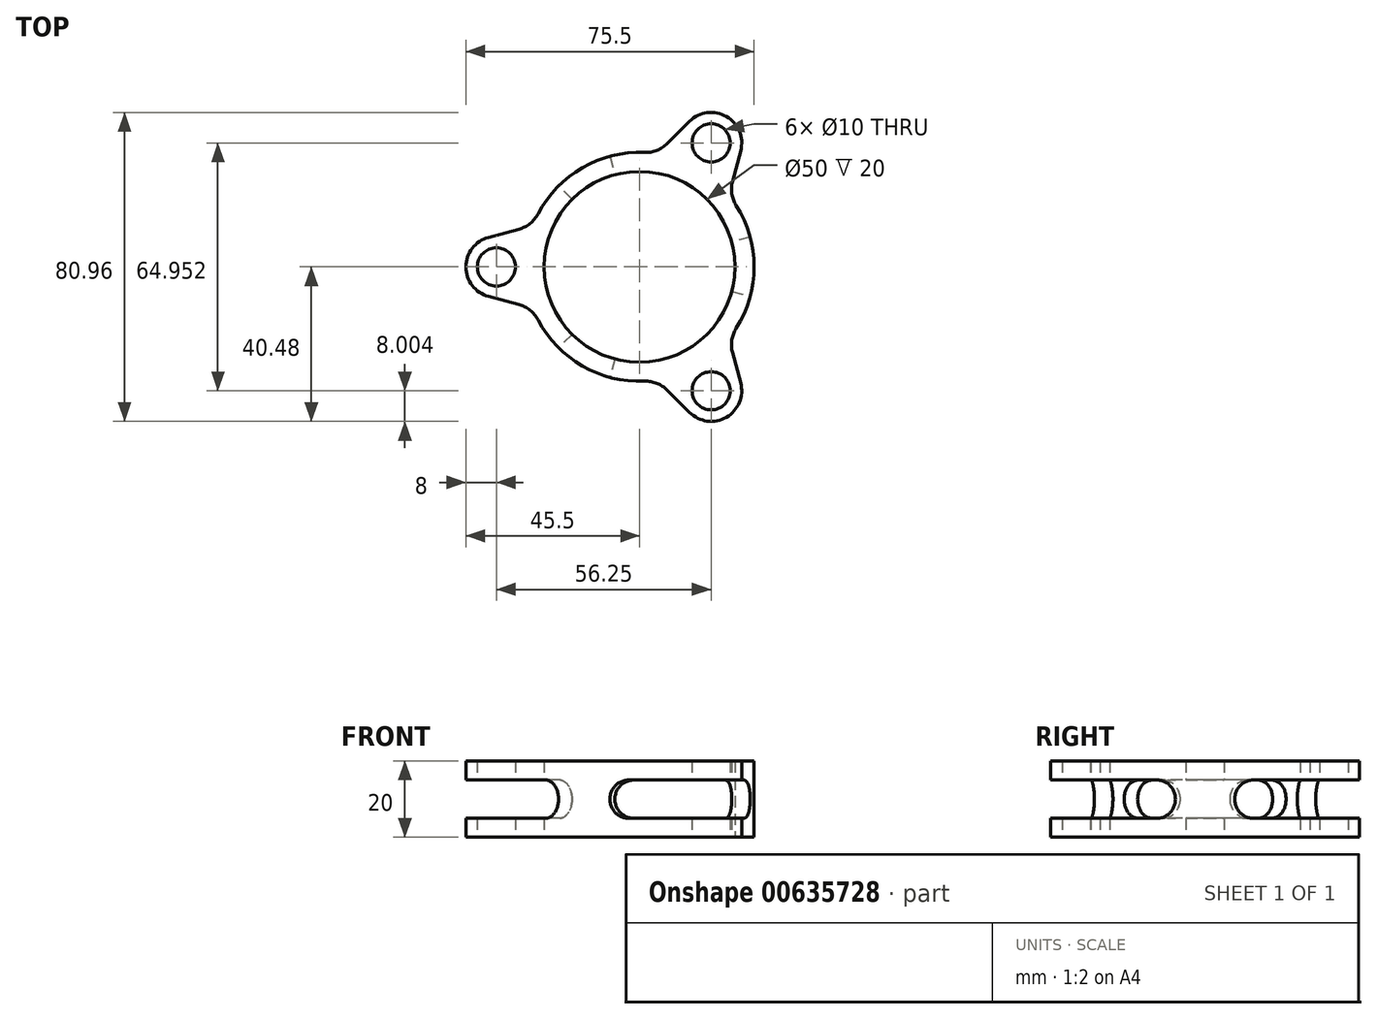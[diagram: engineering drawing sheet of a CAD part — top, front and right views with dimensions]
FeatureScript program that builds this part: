
annotation { "Feature Type Name" : "Feature", "Feature Type Description" : "" }
export const myFeature = defineFeature(function(context is Context, id is Id, definition is map)
    precondition{}
    {
        {
            assignVariable(context, id + "F0", {"name" : "CutoutThickness", "anyValue" : 10});
        }
        {
            assignVariable(context, id + "F1", {"name" : "CutoutFilletRadius", "anyValue" : getVariable(context, 'CutoutThickness') / 2});
        }
        {
            var Q0;
            Q0=qCreatedBy(makeId("Top.planeOp"),FACE);
            var sketch = newSketch(context, id + "F2", { "sketchPlane" : qUnion([Q0])});
            skCircle(sketch, "E0", {"center": v(0, 0) * mm, "radius": 25 * mm});
            skCircle(sketch, "E1", {"center": v(0, 0) * mm, "radius": 30 * mm});
            skLineSegment(sketch, "E2", {"start": v(-75, 0) * mm, "end": v(0, 0) * mm, "construction": true});
            skCircle(sketch, "E3", {"center": v(-37.5, 0) * mm, "radius": 5 * mm});
            skCircle(sketch, "E4", {"center": v(0, 0) * mm, "radius": 37.5 * mm, "construction": true});
            skLineSegment(sketch, "E5", {"start": v(-27.98, 10.83) * mm, "end": v(-39.57, 7.73) * mm});
            skLineSegment(sketch, "E6", {"start": v(-27.98, -10.83) * mm, "end": v(-39.57, -7.73) * mm});
            skArc(sketch, "E7", {"start": v(-39.57, 7.73) * mm, "mid": v(-45.5, 0) * mm, "end": v(-39.57, -7.73) * mm});
            skLineSegment(sketch, "E8.1.0", {"start": v(4.6, -29.64) * mm, "end": v(13.1, -38.13) * mm});
            skCircle(sketch, "E8.1.1", {"center": v(18.75, -32.48) * mm, "radius": 5 * mm});
            skLineSegment(sketch, "E8.1.2", {"start": v(23.37, -18.81) * mm, "end": v(26.48, -30.4) * mm});
            skArc(sketch, "E8.1.3", {"start": v(13.1, -38.13) * mm, "mid": v(22.75, -39.4) * mm, "end": v(26.48, -30.4) * mm});
            skLineSegment(sketch, "E8.2.0", {"start": v(23.37, 18.81) * mm, "end": v(26.48, 30.4) * mm});
            skCircle(sketch, "E8.2.1", {"center": v(18.75, 32.48) * mm, "radius": 5 * mm});
            skLineSegment(sketch, "E8.2.2", {"start": v(4.6, 29.64) * mm, "end": v(13.1, 38.13) * mm});
            skArc(sketch, "E8.2.3", {"start": v(26.48, 30.4) * mm, "mid": v(22.75, 39.4) * mm, "end": v(13.1, 38.13) * mm});
            skLineSegment(sketch, "E9", {"start": v(0, 0) * mm, "end": v(-35.36, 35.36) * mm});
            skLineSegment(sketch, "E10", {"start": v(0, 0) * mm, "end": v(-12.94, 48.3) * mm});
            skLineSegment(sketch, "E11", {"start": v(0, 0) * mm, "end": v(-25, 43.3) * mm, "construction": true});
            skLineSegment(sketch, "E12.1.0", {"start": v(0, 0) * mm, "end": v(-35.36, -35.36) * mm});
            skLineSegment(sketch, "E12.1.1", {"start": v(-12.94, -48.3) * mm, "end": v(0, 0) * mm});
            skLineSegment(sketch, "E12.2.0", {"start": v(0, 0) * mm, "end": v(48.3, -12.94) * mm});
            skLineSegment(sketch, "E12.2.1", {"start": v(0, 0) * mm, "end": v(48.3, 12.94) * mm});
            skSolve(sketch);
        }
        {
            var Q0;
            Q0 = qSketchRegion(id + "F2", true);
            extrude(context, id + "F3", {"entities" : qUnion([Q0]), "endBound" : BoundingType.SYMMETRIC, "depth" : 20 * mm, "offsetDistance" : 25 * mm});
        }
        {
            var Q0;
            Q0=makeQuery(id+"F2.imprint","IMPRINT",FACE,{"disambiguationData":[TD([[makeQuery(id+"F2.imprint","IMPRINT",EDGE,{"derivedFrom":sQuery(id+"F2.wireOp",EDGE,"E3")}),-1.0]])]});
            var Q1;
            {var subQ3=sQuery(id+"F2.wireOp",EDGE,"E9");var subQ7=sQuery(id+"F2.wireOp",EDGE,"E0");var subQ8=makeQuery(id+"F2.imprint","INTERSECT",VERTEX,{"derivedFrom":[subQ7,subQ3]});Q1=makeQuery(id+"F2.imprint","IMPRINT",FACE,{"disambiguationData":[TD([[makeQuery(id+"F2.imprint","IMPRINT",EDGE,{"disambiguationData":[TD([[subQ8,-1.0]])],"derivedFrom":subQ7}),-1.0]])]});}
            var Q2;
            {var subQ5=sQuery(id+"F2.wireOp",EDGE,"E12.1.1");var subQ6=sQuery(id+"F2.wireOp",EDGE,"E0");var subQ7=makeQuery(id+"F2.imprint","INTERSECT",VERTEX,{"derivedFrom":[subQ6,subQ5]});Q2=makeQuery(id+"F2.imprint","IMPRINT",FACE,{"disambiguationData":[TD([[makeQuery(id+"F2.imprint","IMPRINT",EDGE,{"disambiguationData":[TD([[subQ7,-1.0]])],"derivedFrom":subQ6}),-1.0]])]});}
            var Q3;
            {var subQ1=sQuery(id+"F2.wireOp",EDGE,"E8.1.0");Q3=makeQuery(id+"F2.imprint","IMPRINT",FACE,{"disambiguationData":[TD([[makeQuery(id+"F2.imprint","IMPRINT",EDGE,{"derivedFrom":subQ1}),1.0]])]});}
            var Q4;
            {var subQ2=sQuery(id+"F2.wireOp",EDGE,"E10");var subQ6=sQuery(id+"F2.wireOp",EDGE,"E0");var subQ9=makeQuery(id+"F2.imprint","INTERSECT",VERTEX,{"derivedFrom":[subQ6,subQ2]});Q4=makeQuery(id+"F2.imprint","IMPRINT",FACE,{"disambiguationData":[TD([[makeQuery(id+"F2.imprint","IMPRINT",EDGE,{"disambiguationData":[TD([[subQ9,1.0]])],"derivedFrom":subQ6}),-1.0]])]});}
            var Q5;
            {var subQ1=sQuery(id+"F2.wireOp",EDGE,"E8.2.0");Q5=makeQuery(id+"F2.imprint","IMPRINT",FACE,{"disambiguationData":[TD([[makeQuery(id+"F2.imprint","IMPRINT",EDGE,{"derivedFrom":subQ1}),1.0]])]});}
            extrude(context, id + "F4", {"entities" : qUnion([Q0, Q1, Q2, Q3, Q4, Q5]), "operationType" : NewBodyOperationType.REMOVE, "endBound" : BoundingType.SYMMETRIC, "oppositeDirection" : true, "depth" : (getVariable(context, 'CutoutThickness')) * mm, "offsetDistance" : 25 * mm});
        }
        {
            var Q0;
            Q0=makeQuery(id+"F3.opExtrude","SWEPT_EDGE",EDGE,{"disambiguationData":[OSD([sQuery(id+"F2.wireOp",EDGE,"E1"),sQuery(id+"F2.wireOp",EDGE,"E6")])]});
            var Q1;
            Q1=makeQuery(id+"F3.opExtrude","SWEPT_EDGE",EDGE,{"disambiguationData":[OSD([sQuery(id+"F2.wireOp",EDGE,"E1"),sQuery(id+"F2.wireOp",EDGE,"E8.1.0")])]});
            var Q2;
            Q2=makeQuery(id+"F3.opExtrude","SWEPT_EDGE",EDGE,{"disambiguationData":[OSD([sQuery(id+"F2.wireOp",EDGE,"E1"),sQuery(id+"F2.wireOp",EDGE,"E8.1.2")])]});
            var Q3;
            Q3=makeQuery(id+"F3.opExtrude","SWEPT_EDGE",EDGE,{"disambiguationData":[OSD([sQuery(id+"F2.wireOp",EDGE,"E1"),sQuery(id+"F2.wireOp",EDGE,"E8.2.0")])]});
            var Q4;
            Q4=makeQuery(id+"F3.opExtrude","SWEPT_EDGE",EDGE,{"disambiguationData":[OSD([sQuery(id+"F2.wireOp",EDGE,"E1"),sQuery(id+"F2.wireOp",EDGE,"E8.2.2")])]});
            var Q5;
            Q5=makeQuery(id+"F3.opExtrude","SWEPT_EDGE",EDGE,{"disambiguationData":[OSD([sQuery(id+"F2.wireOp",EDGE,"E1"),sQuery(id+"F2.wireOp",EDGE,"E5")])]});
            fillet(context, id + "F5", {"entities" : qUnion([Q0, Q1, Q2, Q3, Q4, Q5]), "radius" : 8 * mm, "tangentPropagation" : true, "allowEdgeOverflow" : false});
        }
        {
            var Q0;
            Q0=makeQuery(id+"F4.boolean.opBoolean","COPY",EDGE,{"derivedFrom":makeQuery(id+"F4.opExtrude","CAP_EDGE",EDGE,{"disambiguationData":[OSD([sQuery(id+"F2.wireOp",EDGE,"E12.1.0")])],"isStart":true})});
            var Q1;
            Q1=makeQuery(id+"F4.boolean.opBoolean","COPY",EDGE,{"derivedFrom":makeQuery(id+"F4.opExtrude","CAP_EDGE",EDGE,{"disambiguationData":[OSD([sQuery(id+"F2.wireOp",EDGE,"E12.1.0")])],"isStart":false})});
            var Q2;
            Q2=makeQuery(id+"F4.boolean.opBoolean","COPY",EDGE,{"derivedFrom":makeQuery(id+"F4.opExtrude","CAP_EDGE",EDGE,{"disambiguationData":[OSD([sQuery(id+"F2.wireOp",EDGE,"E12.1.1")])],"isStart":false})});
            var Q3;
            Q3=makeQuery(id+"F4.boolean.opBoolean","COPY",EDGE,{"derivedFrom":makeQuery(id+"F4.opExtrude","CAP_EDGE",EDGE,{"disambiguationData":[OSD([sQuery(id+"F2.wireOp",EDGE,"E12.1.1")])],"isStart":true})});
            var Q4;
            Q4=makeQuery(id+"F4.boolean.opBoolean","COPY",EDGE,{"derivedFrom":makeQuery(id+"F4.opExtrude","CAP_EDGE",EDGE,{"disambiguationData":[OSD([sQuery(id+"F2.wireOp",EDGE,"E12.2.0")])],"isStart":true})});
            var Q5;
            Q5=makeQuery(id+"F4.boolean.opBoolean","COPY",EDGE,{"derivedFrom":makeQuery(id+"F4.opExtrude","CAP_EDGE",EDGE,{"disambiguationData":[OSD([sQuery(id+"F2.wireOp",EDGE,"E12.2.0")])],"isStart":false})});
            var Q6;
            Q6=makeQuery(id+"F4.boolean.opBoolean","COPY",EDGE,{"derivedFrom":makeQuery(id+"F4.opExtrude","CAP_EDGE",EDGE,{"disambiguationData":[OSD([sQuery(id+"F2.wireOp",EDGE,"E12.2.1")])],"isStart":true})});
            var Q7;
            Q7=makeQuery(id+"F4.boolean.opBoolean","COPY",EDGE,{"derivedFrom":makeQuery(id+"F4.opExtrude","CAP_EDGE",EDGE,{"disambiguationData":[OSD([sQuery(id+"F2.wireOp",EDGE,"E12.2.1")])],"isStart":false})});
            var Q8;
            Q8=makeQuery(id+"F4.boolean.opBoolean","COPY",EDGE,{"derivedFrom":makeQuery(id+"F4.opExtrude","CAP_EDGE",EDGE,{"disambiguationData":[OSD([sQuery(id+"F2.wireOp",EDGE,"E10")])],"isStart":false})});
            var Q9;
            Q9=makeQuery(id+"F4.boolean.opBoolean","COPY",EDGE,{"derivedFrom":makeQuery(id+"F4.opExtrude","CAP_EDGE",EDGE,{"disambiguationData":[OSD([sQuery(id+"F2.wireOp",EDGE,"E10")])],"isStart":true})});
            var Q10;
            Q10=makeQuery(id+"F4.boolean.opBoolean","COPY",EDGE,{"derivedFrom":makeQuery(id+"F4.opExtrude","CAP_EDGE",EDGE,{"disambiguationData":[OSD([sQuery(id+"F2.wireOp",EDGE,"E9")])],"isStart":false})});
            var Q11;
            Q11=makeQuery(id+"F4.boolean.opBoolean","COPY",EDGE,{"derivedFrom":makeQuery(id+"F4.opExtrude","CAP_EDGE",EDGE,{"disambiguationData":[OSD([sQuery(id+"F2.wireOp",EDGE,"E9")])],"isStart":true})});
            fillet(context, id + "F6", {"entities" : qUnion([Q0, Q1, Q2, Q3, Q4, Q5, Q6, Q7, Q8, Q9, Q10, Q11]), "radius" : (getVariable(context, 'CutoutFilletRadius')) * mm, "tangentPropagation" : true, "allowEdgeOverflow" : false});
        }
    });
